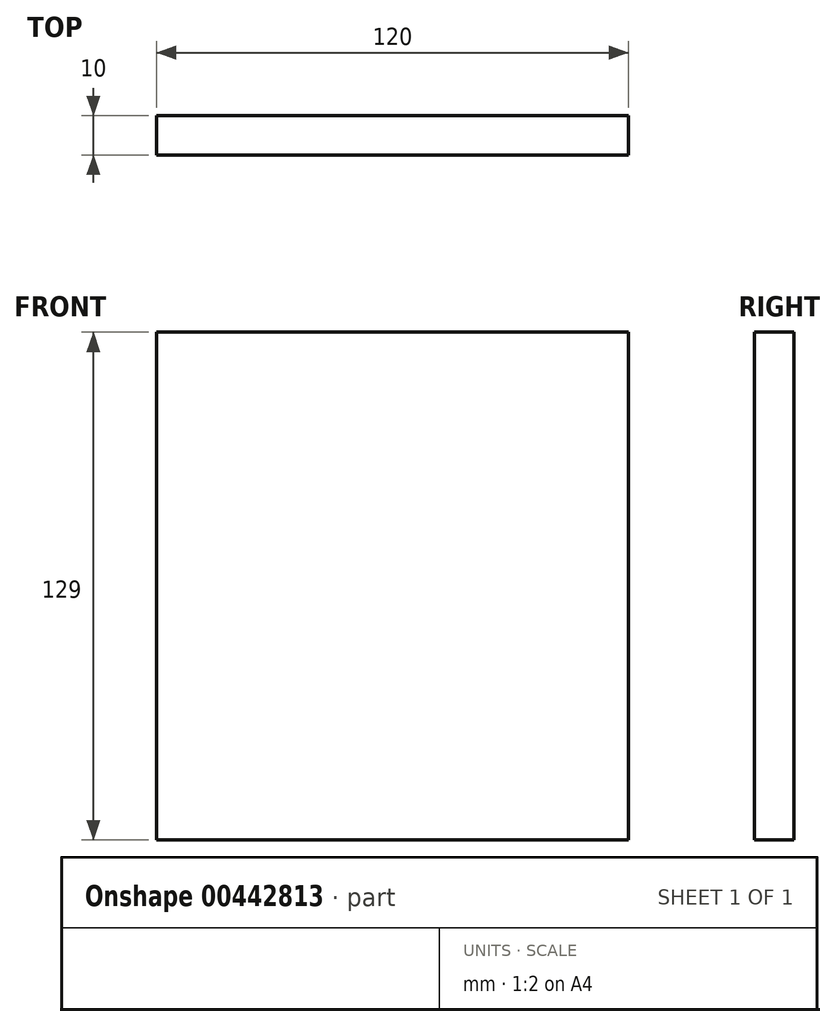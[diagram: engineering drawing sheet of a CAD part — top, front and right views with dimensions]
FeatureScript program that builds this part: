
annotation { "Feature Type Name" : "Feature", "Feature Type Description" : "" }
export const myFeature = defineFeature(function(context is Context, id is Id, definition is map)
    precondition{}
    {
        {
            var Q0;
            Q0=qCreatedBy(makeId("Front.planeOp"),FACE);
            var sketch = newSketch(context, id + "F0", { "sketchPlane" : qUnion([Q0])});
            skLineSegment(sketch, "E0.bottom", {"start": v(0, 0) * mm, "end": v(-120, 0) * mm});
            skLineSegment(sketch, "E0.top", {"start": v(0, 129) * mm, "end": v(-120, 129) * mm});
            skLineSegment(sketch, "E0.left", {"start": v(0, 0) * mm, "end": v(0, 129) * mm});
            skLineSegment(sketch, "E0.right", {"start": v(-120, 0) * mm, "end": v(-120, 129) * mm});
            skSolve(sketch);
        }
        {
            var Q0;
            Q0 = qSketchRegion(id + "F0", true);
            extrude(context, id + "F1", {"entities" : qUnion([Q0]), "depth" : 10 * mm, "offsetDistance" : 25 * mm});
        }
    });
